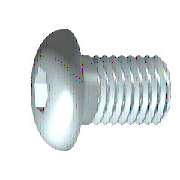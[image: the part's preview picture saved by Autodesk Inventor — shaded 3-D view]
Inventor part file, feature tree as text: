
AUTODESK INVENTOR PART (.ipt)
format: ipt  version: 2025 (Build 290162010, 162A)  size: 185,344 bytes
history: native  units: mm (DEFAULTED — no unit token found)
features: extrude x1, plane x1, fillet x1
ambient origin geometry x7: Origin, YZ Plane, XY Plane, X Axis, Y Axis, Z Axis, Center Point
bodies: Solid1 (feature_tree), Body (feature_tree)
feature tree (3):
  extrude  "Slot"  Depth=18.0mm
  plane  "Work Plane1"
  fillet  "Fillet2"  Radius=0.306825mm
